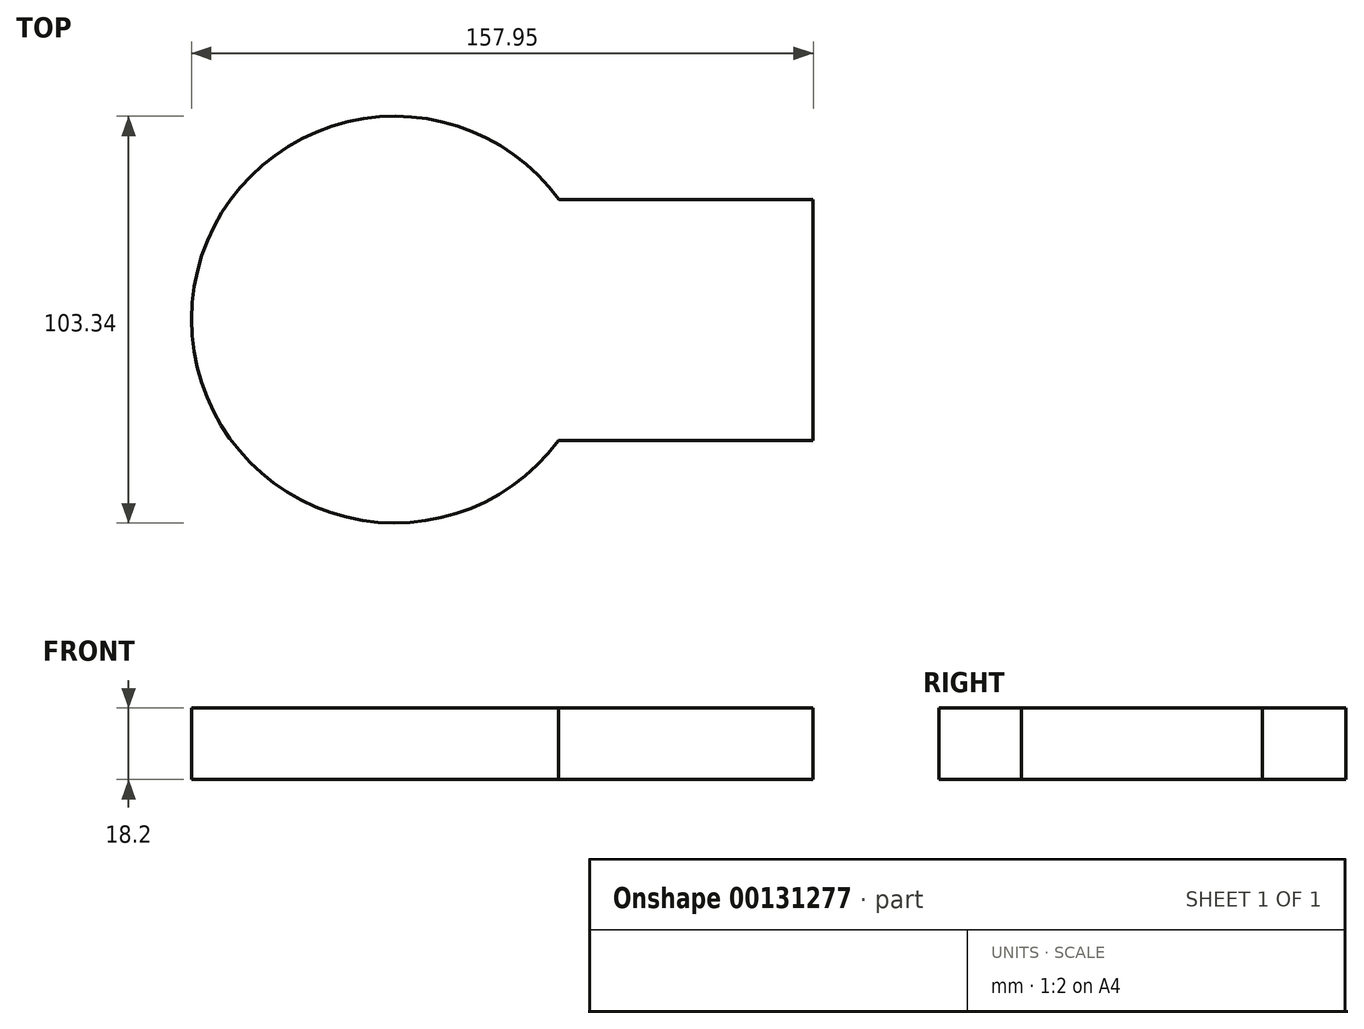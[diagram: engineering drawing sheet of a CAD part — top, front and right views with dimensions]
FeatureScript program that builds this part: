
annotation { "Feature Type Name" : "Feature", "Feature Type Description" : "" }
export const myFeature = defineFeature(function(context is Context, id is Id, definition is map)
    precondition{}
    {
        {
            var Q0;
            Q0=qCreatedBy(makeId("Top.planeOp"),FACE);
            var sketch = newSketch(context, id + "F0", { "sketchPlane" : qUnion([Q0])});
            skLineSegment(sketch, "E0.bottom", {"start": v(-16.43, 30.48) * mm, "end": v(48.12, 30.48) * mm});
            skLineSegment(sketch, "E0.top", {"start": v(-16.64, -30.76) * mm, "end": v(48.12, -30.76) * mm});
            skLineSegment(sketch, "E0.right", {"start": v(48.12, 30.48) * mm, "end": v(48.12, -30.76) * mm});
            skArc(sketch, "E1", {"start": v(-16.43, 30.48) * mm, "mid": v(-109.83, 0.18) * mm, "end": v(-16.64, -30.76) * mm});
            skSolve(sketch);
        }
        {
            var Q0;
            Q0=makeQuery(id+"F0.imprint","IMPRINT",FACE,{"disambiguationData":[TD([[makeQuery(id+"F0.imprint","IMPRINT",EDGE,{"derivedFrom":sQuery(id+"F0.wireOp",EDGE,"E0.bottom")}),-1.0]])]});
            extrude(context, id + "F1", {"entities" : qUnion([Q0]), "depth" : 18.2 * mm});
        }
    });
